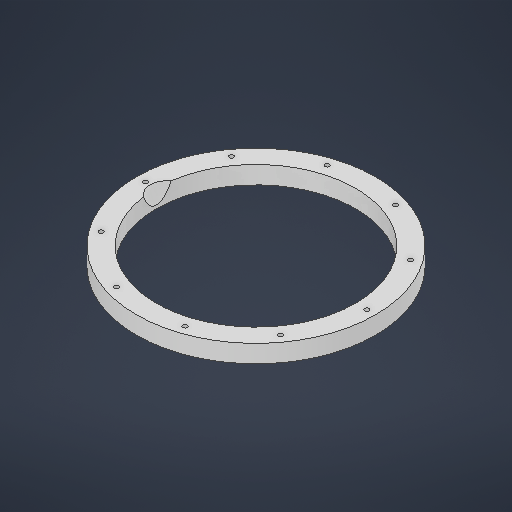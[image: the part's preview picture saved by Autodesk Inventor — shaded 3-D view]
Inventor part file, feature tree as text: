
AUTODESK INVENTOR PART (.ipt)
format: ipt  version: 2025 (Build 290162000, 162)  size: 226,304 bytes
history: native  units: in
note: dims shown in document units (in); Inventor stores cm internally (conversion verified against a paired STEP export)
features: sketch x4, extrude x2, plane x2, hole x1
ambient origin geometry x8: Origin, YZ Plane, XZ Plane, XY Plane, X Axis, Y Axis, Z Axis, Center Point
bodies: Solid1 (feature_tree)
feature tree (9):
  extrude  "Extrusion1"  Depth=8.8583in
  hole  "Hole1"  [1 undecoded]
  plane  "Work Plane6"
  plane  "Work Plane7"
  extrude  "Extrusion4"  Depth=3.937in TaperAngle=360.0deg
  sketch  "Sketch1"  dims[d0=10.6299in d1=8.8583in]
  sketch  "Sketch3"  dims[d8=0.1969in d9=3.937in d11=360.0deg]
  sketch  "Sketch Circular Pattern1"  dims[d2=0.7874in d3=0.0in d7=9.8425in]
  sketch  "Sketch5"  dims[d13=0.1969in d14=0.2362in d15=0.1575in d16=0.0787in d17=90.0deg d18=0.315in d19=0.8108in d25=2.5in d26=1.5748in d27=3.3802in d28=9.8937in d29=0.0in]
note: 1 required parameter value undecoded (feature->parameter linkage not recoverable at this tier; creation-order binding heuristic only, values carry confidence <= 0.55)
